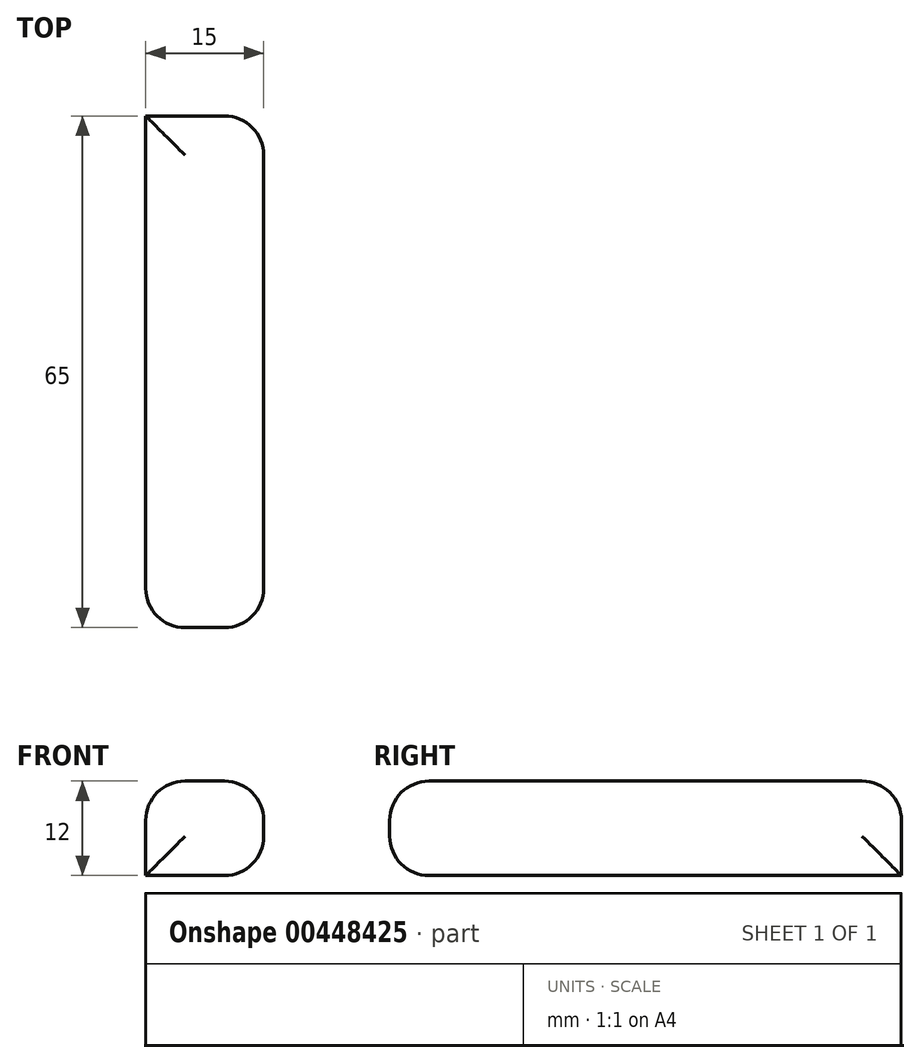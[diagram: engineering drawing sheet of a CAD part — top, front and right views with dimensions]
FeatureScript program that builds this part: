
annotation { "Feature Type Name" : "Feature", "Feature Type Description" : "" }
export const myFeature = defineFeature(function(context is Context, id is Id, definition is map)
    precondition{}
    {
        {
            var Q0;
            Q0=qCreatedBy(makeId("Top.planeOp"),FACE);
            var sketch = newSketch(context, id + "F0", { "sketchPlane" : qUnion([Q0])});
            skLineSegment(sketch, "E0.bottom", {"start": v(7.5, -32.5) * mm, "end": v(-7.5, -32.5) * mm});
            skLineSegment(sketch, "E0.top", {"start": v(7.5, 32.5) * mm, "end": v(-7.5, 32.5) * mm});
            skLineSegment(sketch, "E0.left", {"start": v(7.5, -32.5) * mm, "end": v(7.5, 32.5) * mm});
            skLineSegment(sketch, "E0.right", {"start": v(-7.5, -32.5) * mm, "end": v(-7.5, 32.5) * mm});
            skPoint(sketch, "E0.middle", {"position": v(0, 0) * mm});
            skSolve(sketch);
        }
        {
            var Q0;
            Q0=makeQuery(id+"F0.imprint","IMPRINT",FACE,{"disambiguationData":[TD([[makeQuery(id+"F0.imprint","IMPRINT",EDGE,{"derivedFrom":sQuery(id+"F0.wireOp",EDGE,"E0.bottom")}),-1.0]])]});
            extrude(context, id + "F1", {"entities" : qUnion([Q0]), "depth" : 12 * mm});
        }
        {
            var Q0;
            Q0=makeQuery(id+"F1.opExtrude","SWEPT_FACE",FACE,{"disambiguationData":[OSD([sQuery(id+"F0.wireOp",EDGE,"E0.left")])]});
            var Q1;
            Q1=makeQuery(id+"F1.opExtrude","CAP_FACE",FACE,{"disambiguationData":[OSD([sQuery(id+"F0.wireOp",EDGE,"E0.bottom"),sQuery(id+"F0.wireOp",EDGE,"E0.top"),sQuery(id+"F0.wireOp",EDGE,"E0.left"),sQuery(id+"F0.wireOp",EDGE,"E0.right")])],"isStart":false});
            var Q2;
            Q2=makeQuery(id+"F1.opExtrude","SWEPT_FACE",FACE,{"disambiguationData":[OSD([sQuery(id+"F0.wireOp",EDGE,"E0.bottom")])]});
            fillet(context, id + "F2", {"entities" : qUnion([Q0, Q1, Q2]), "radius" : 5 * mm, "tangentPropagation" : true, "allowEdgeOverflow" : false});
        }
    });
